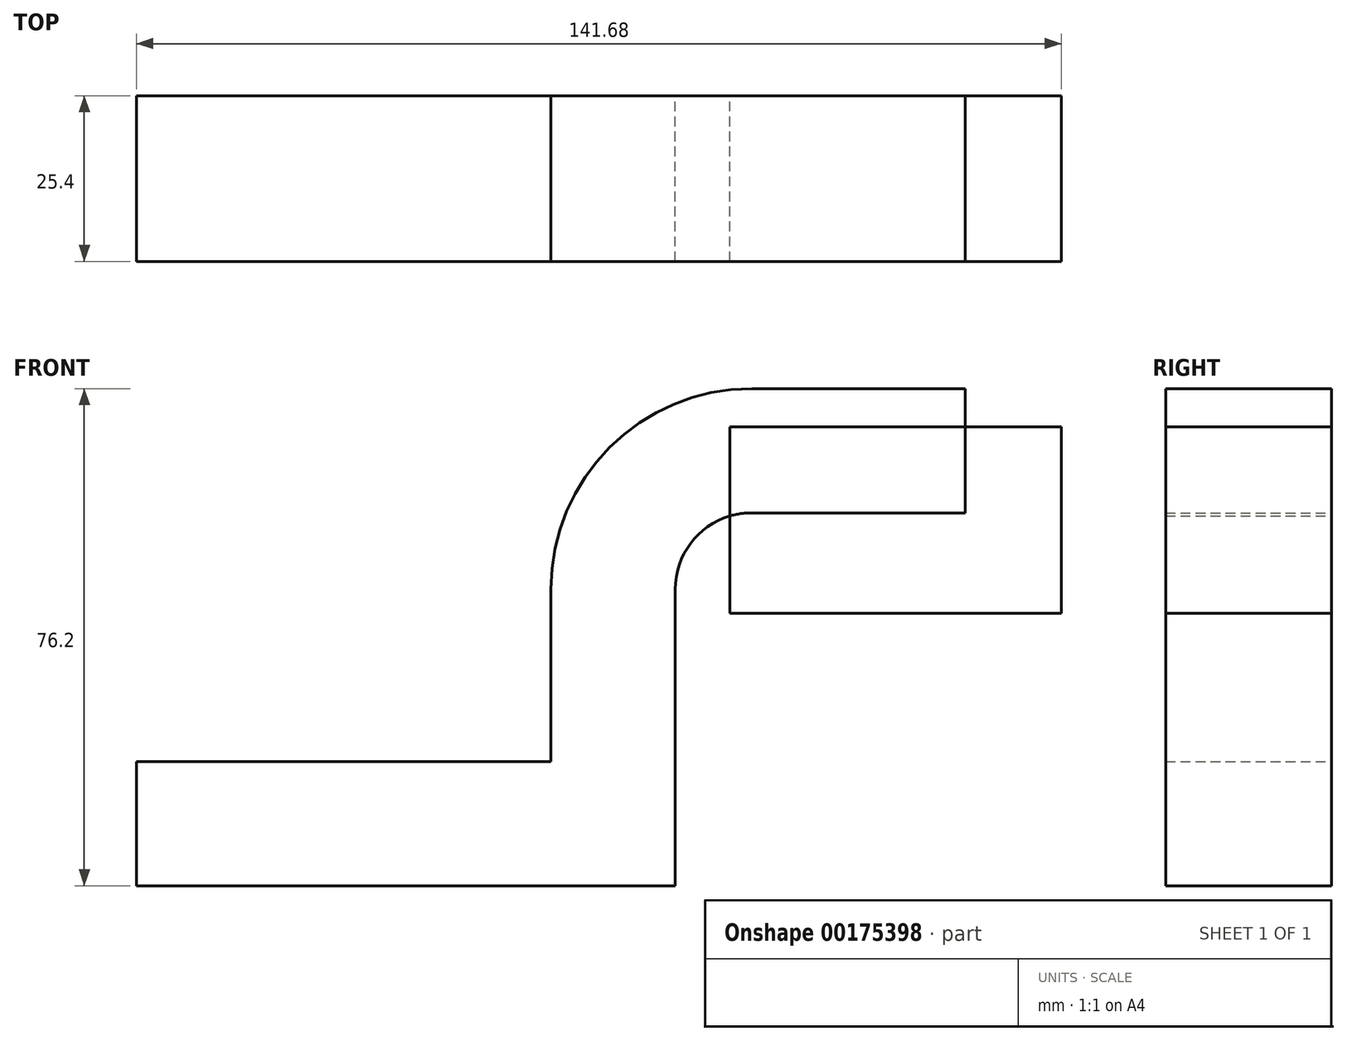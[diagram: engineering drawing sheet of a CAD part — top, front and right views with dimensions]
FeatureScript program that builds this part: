
annotation { "Feature Type Name" : "Feature", "Feature Type Description" : "" }
export const myFeature = defineFeature(function(context is Context, id is Id, definition is map)
    precondition{}
    {
        {
            var Q0;
            Q0=qCreatedBy(makeId("Front.planeOp"),FACE);
            var sketch = newSketch(context, id + "F0", { "sketchPlane" : qUnion([Q0])});
            skLineSegment(sketch, "E0.bottom", {"start": v(41.28, 9.53) * mm, "end": v(-41.28, 9.53) * mm});
            skLineSegment(sketch, "E0.top", {"start": v(41.28, -9.52) * mm, "end": v(-41.28, -9.52) * mm});
            skLineSegment(sketch, "E0.left", {"start": v(41.28, 9.53) * mm, "end": v(41.28, -9.52) * mm});
            skLineSegment(sketch, "E0.right", {"start": v(-41.28, 9.53) * mm, "end": v(-41.28, -9.52) * mm});
            skPoint(sketch, "E0.middle", {"position": v(0, 0) * mm});
            skLineSegment(sketch, "E1.bottom", {"start": v(100.41, 60.78) * mm, "end": v(49.61, 60.78) * mm});
            skLineSegment(sketch, "E1.top", {"start": v(100.41, 32.2) * mm, "end": v(49.61, 32.2) * mm});
            skLineSegment(sketch, "E1.left", {"start": v(100.41, 60.78) * mm, "end": v(100.41, 32.2) * mm});
            skLineSegment(sketch, "E1.right", {"start": v(49.61, 60.78) * mm, "end": v(49.61, 32.2) * mm});
            skPoint(sketch, "E1.middle", {"position": v(75.01, 46.5) * mm});
            skLineSegment(sketch, "E2", {"start": v(41.28, 9.53) * mm, "end": v(41.28, 35.93) * mm});
            skArc(sketch, "E3", {"start": v(41.27, 35.93) * mm, "mid": v(44.7, 44.2) * mm, "end": v(52.97, 47.63) * mm});
            skLineSegment(sketch, "E4", {"start": v(52.97, 47.63) * mm, "end": v(85.72, 47.63) * mm});
            skLineSegment(sketch, "E5.0", {"start": v(52.97, 66.68) * mm, "end": v(85.72, 66.68) * mm});
            skArc(sketch, "E5.1", {"start": v(22.22, 35.93) * mm, "mid": v(31.23, 57.67) * mm, "end": v(52.97, 66.68) * mm});
            skLineSegment(sketch, "E5.2", {"start": v(22.22, 9.53) * mm, "end": v(22.22, 35.93) * mm});
            skLineSegment(sketch, "E6", {"start": v(85.72, 47.63) * mm, "end": v(85.72, 66.68) * mm});
            skFitSpline(sketch, "E7", {"points": [v(-41.28, 9.52) * mm, v(52.97, 66.68) * mm], "startDerivative": vector(23.09, 100.64) * mm, "endDerivative": vector(104.88, -14.37) * mm});
            skSolve(sketch);
        }
        {
            var Q0;
            Q0=makeQuery(id+"F0.imprint","IMPRINT",FACE,{"disambiguationData":[TD([[makeQuery(id+"F0.imprint","IMPRINT",EDGE,{"derivedFrom":sQuery(id+"F0.wireOp",EDGE,"E0.top")}),-1.0]])]});
            var Q1;
            Q1=makeQuery(id+"F0.imprint","IMPRINT",FACE,{"disambiguationData":[TD([[makeQuery(id+"F0.imprint","IMPRINT",EDGE,{"derivedFrom":sQuery(id+"F0.wireOp",EDGE,"E5.1")}),1.0]])]});
            var Q2;
            {var subQ0=sQuery(id+"F0.wireOp",EDGE,"E2");Q2=makeQuery(id+"F0.imprint","IMPRINT",FACE,{"disambiguationData":[TD([[makeQuery(id+"F0.imprint","IMPRINT",EDGE,{"derivedFrom":subQ0}),1.0]])]});}
            var Q3;
            {var subQ1=sQuery(id+"F0.wireOp",EDGE,"E1.top");Q3=makeQuery(id+"F0.imprint","IMPRINT",FACE,{"disambiguationData":[TD([[makeQuery(id+"F0.imprint","IMPRINT",EDGE,{"derivedFrom":subQ1}),-1.0]])]});}
            extrude(context, id + "F1", {"entities" : qUnion([Q0, Q1, Q2, Q3]), "depth" : 25.4 * mm});
        }
    });
